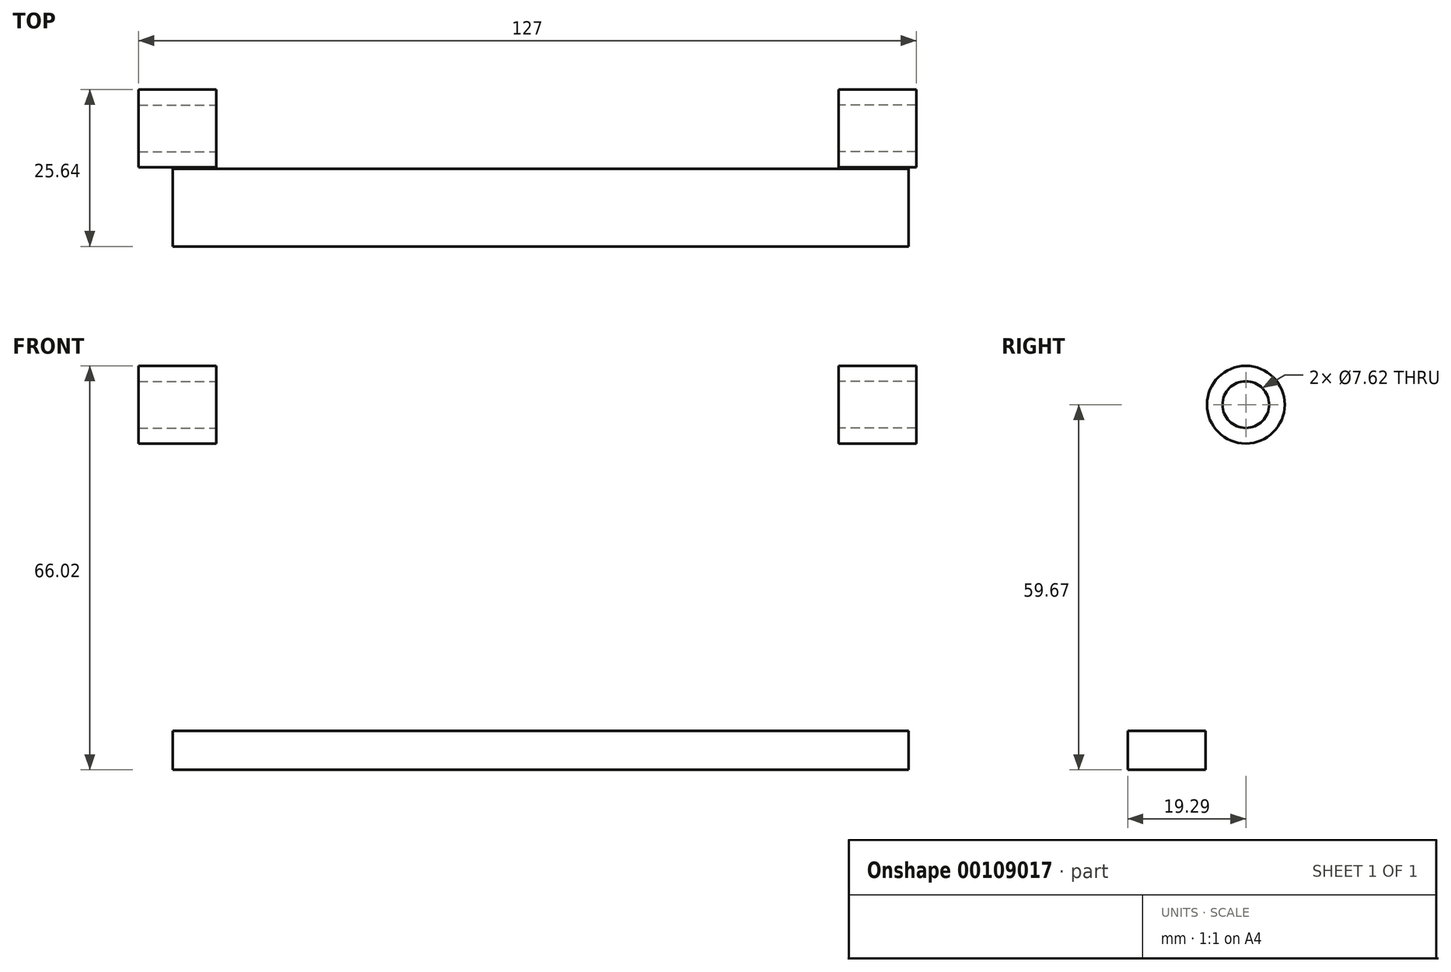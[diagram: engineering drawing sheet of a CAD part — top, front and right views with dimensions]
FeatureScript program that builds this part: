
annotation { "Feature Type Name" : "Feature", "Feature Type Description" : "" }
export const myFeature = defineFeature(function(context is Context, id is Id, definition is map)
    precondition{}
    {
        {
            var Q0;
            Q0=qCreatedBy(makeId("Right.planeOp"),FACE);
            var sketch = newSketch(context, id + "F0", { "sketchPlane" : qUnion([Q0])});
            skCircle(sketch, "E0", {"center": v(0, 0) * mm, "radius": 3.81 * mm});
            skCircle(sketch, "E1", {"center": v(0, 0) * mm, "radius": 6.35 * mm});
            skLineSegment(sketch, "E2", {"start": v(0, 0) * mm, "end": v(-6.35, 0) * mm});
            skLineSegment(sketch, "E3", {"start": v(-6.35, 0) * mm, "end": v(-19.05, 0) * mm});
            skLineSegment(sketch, "E4", {"start": v(-19.05, 0) * mm, "end": v(-6.35, 0) * mm});
            skLineSegment(sketch, "E5", {"start": v(0, -6.35) * mm, "end": v(-11.46, -6.35) * mm});
            skLineSegment(sketch, "E6", {"start": v(-19.05, 0) * mm, "end": v(-19.29, -59.67) * mm});
            skLineSegment(sketch, "E7", {"start": v(-11.46, -6.35) * mm, "end": v(-11.67, -59.67) * mm});
            skLineSegment(sketch, "E8", {"start": v(-19.29, -59.67) * mm, "end": v(-11.67, -59.67) * mm});
            skLineSegment(sketch, "E9", {"start": v(-19.29, -59.67) * mm, "end": v(-19.29, -53.32) * mm});
            skLineSegment(sketch, "E10", {"start": v(-19.29, -53.32) * mm, "end": v(-6.59, -53.32) * mm});
            skLineSegment(sketch, "E11", {"start": v(-6.59, -53.32) * mm, "end": v(-6.59, -59.67) * mm});
            skLineSegment(sketch, "E12", {"start": v(-6.59, -59.67) * mm, "end": v(-11.67, -59.67) * mm});
            skSolve(sketch);
        }
        {
            var Q0;
            Q0=makeQuery(id+"F0.imprint","IMPRINT",FACE,{"disambiguationData":[TD([[makeQuery(id+"F0.imprint","IMPRINT",EDGE,{"derivedFrom":sQuery(id+"F0.wireOp",EDGE,"E0")}),-1.0]])]});
            extrude(context, id + "F1", {"entities" : qUnion([Q0]), "depth" : 6.35 * mm, "hasSecondDirection" : true, "secondDirectionOppositeDirection" : true, "secondDirectionDepth" : 6.35 * mm});
        }
        {
            var Q0;
            {var subQ1=sQuery(id+"F0.wireOp",EDGE,"E4");Q0=makeQuery(id+"F0.imprint","IMPRINT",FACE,{"disambiguationData":[TD([[makeQuery(id+"F0.imprint","IMPRINT",EDGE,{"derivedFrom":subQ1}),-1.0]])]});}
            var Q1;
            {var subQ0=sQuery(id+"F0.wireOp",EDGE,"E9");Q1=makeQuery(id+"F0.imprint","IMPRINT",FACE,{"disambiguationData":[TD([[makeQuery(id+"F0.imprint","IMPRINT",EDGE,{"derivedFrom":subQ0}),-1.0]])]});}
            var Q2;
            {var subQ0=sQuery(id+"F0.wireOp",EDGE,"E8");Q2=makeQuery(id+"F0.imprint","IMPRINT",FACE,{"disambiguationData":[TD([[makeQuery(id+"F0.imprint","IMPRINT",EDGE,{"derivedFrom":subQ0}),1.0]])]});}
            var Q3;
            {var subQ4=sQuery(id+"F0.wireOp",EDGE,"E11");Q3=makeQuery(id+"F0.imprint","IMPRINT",FACE,{"disambiguationData":[TD([[makeQuery(id+"F0.imprint","IMPRINT",EDGE,{"derivedFrom":subQ4}),-1.0]])]});}
            extrude(context, id + "F2", {"entities" : qUnion([Q0, Q1, Q2, Q3]), "operationType" : NewBodyOperationType.ADD, "depth" : 5.08 * mm, "hasSecondDirection" : true, "secondDirectionOppositeDirection" : true, "secondDirectionDepth" : 5.08 * mm});
        }
        {
            var Q0;
            Q0=qCreatedBy(makeId("Right.planeOp"),FACE);
            cPlane(context, id + "F3", {"entities" : qUnion([Q0]), "cplaneType" : CPlaneType.OFFSET, "offset" : 57.15 * mm, "oppositeDirection" : true, "width" : 152.4 * mm, "height" : 152.4 * mm});
        }
        {
            var Q0;
            Q0=makeQuery(id+"F1.opExtrude","SWEPT_BODY",BODY,{"disambiguationData":[OSD([sQuery(id+"F0.wireOp",EDGE,"E0"),sQuery(id+"F0.wireOp",EDGE,"E1")])]});
            var Q1;
            Q1=qCreatedBy(id+"F3.planeOp",FACE);
            mirror(context, id + "F4", {"entities" : qUnion([Q0]), "mirrorPlane" : qUnion([Q1])});
        }
        {
            var Q0;
            Q0=makeQuery(id+"F2.opExtrude","CAP_FACE",FACE,{"disambiguationData":[OSD([sQuery(id+"F0.wireOp",EDGE,"E1"),sQuery(id+"F0.wireOp",EDGE,"E4"),sQuery(id+"F0.wireOp",EDGE,"E5"),sQuery(id+"F0.wireOp",EDGE,"E6"),sQuery(id+"F0.wireOp",EDGE,"E7"),sQuery(id+"F0.wireOp",EDGE,"E8"),sQuery(id+"F0.wireOp",EDGE,"E9"),sQuery(id+"F0.wireOp",EDGE,"E10"),sQuery(id+"F0.wireOp",EDGE,"E11"),sQuery(id+"F0.wireOp",EDGE,"E12")])],"isStart":false});
            var sketch = newSketch(context, id + "F5", { "sketchPlane" : qUnion([Q0])});
            skLineSegment(sketch, "E13", {"start": v(-19.26, -53.32) * mm, "end": v(-11.64, -53.32) * mm});
            skSolve(sketch);
        }
        {
            var Q0;
            Q0=makeQuery(id+"F5.imprint","IMPRINT",FACE,{"disambiguationData":[TD([[makeQuery(id+"F5.imprint","IMPRINT",EDGE,{"derivedFrom":sQuery(id+"F5.wireOp",EDGE,"E13")}),-1.0]])]});
            extrude(context, id + "F6", {"entities" : qUnion([Q0]), "operationType" : NewBodyOperationType.ADD, "oppositeDirection" : true, "depth" : 120.14 * mm});
        }
    });
